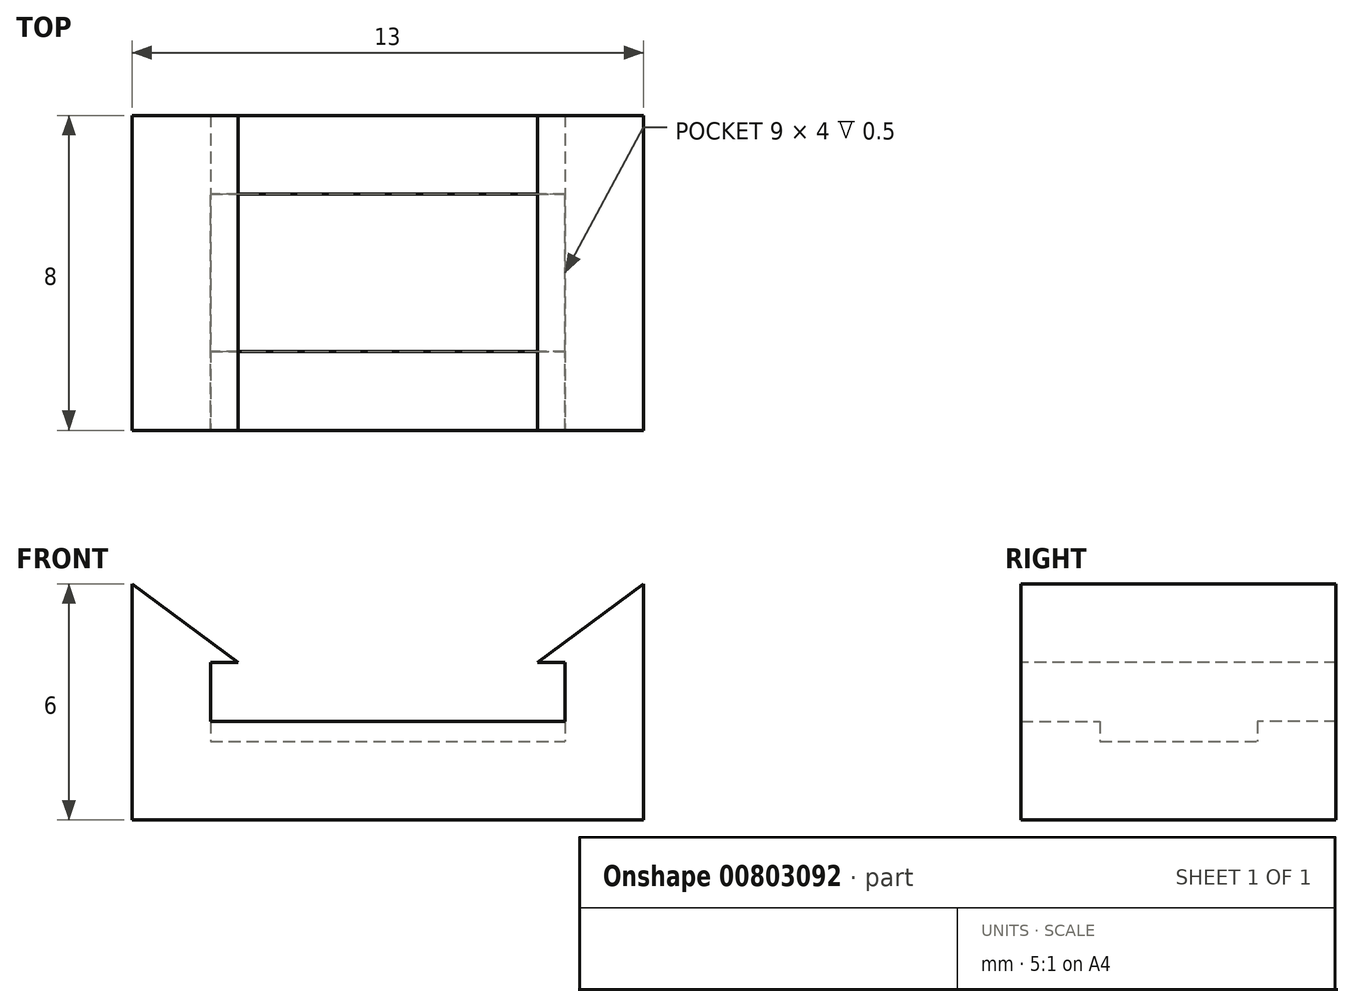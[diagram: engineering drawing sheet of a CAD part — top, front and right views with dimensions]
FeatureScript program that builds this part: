
annotation { "Feature Type Name" : "Feature", "Feature Type Description" : "" }
export const myFeature = defineFeature(function(context is Context, id is Id, definition is map)
    precondition{}
    {
        {
            var Q0;
            Q0=qCreatedBy(makeId("Top.planeOp"),FACE);
            var sketch = newSketch(context, id + "F0", { "sketchPlane" : qUnion([Q0])});
            skLineSegment(sketch, "E0.bottom", {"start": v(6.5, 4) * mm, "end": v(-6.5, 4) * mm});
            skLineSegment(sketch, "E0.top", {"start": v(6.5, -4) * mm, "end": v(-6.5, -4) * mm});
            skLineSegment(sketch, "E0.left", {"start": v(6.5, 4) * mm, "end": v(6.5, -4) * mm});
            skLineSegment(sketch, "E0.right", {"start": v(-6.5, 4) * mm, "end": v(-6.5, -4) * mm});
            skPoint(sketch, "E0.middle", {"position": v(0, 0) * mm});
            skSolve(sketch);
        }
        {
            var Q0;
            Q0=qCreatedBy(makeId("Top.planeOp"),FACE);
            var sketch = newSketch(context, id + "F1", { "sketchPlane" : qUnion([Q0])});
            skLineSegment(sketch, "E1.bottom", {"start": v(6.5, 4) * mm, "end": v(-6.5, 4) * mm});
            skLineSegment(sketch, "E1.top", {"start": v(6.5, -4) * mm, "end": v(-6.5, -4) * mm});
            skLineSegment(sketch, "E1.left", {"start": v(6.5, 4) * mm, "end": v(6.5, -4) * mm});
            skLineSegment(sketch, "E1.right", {"start": v(-6.5, 4) * mm, "end": v(-6.5, -4) * mm});
            skPoint(sketch, "E1.middle", {"position": v(0, 0) * mm});
            skLineSegment(sketch, "E2.bottom", {"start": v(4.5, 2) * mm, "end": v(-4.5, 2) * mm});
            skLineSegment(sketch, "E2.top", {"start": v(4.5, -2) * mm, "end": v(-4.5, -2) * mm});
            skLineSegment(sketch, "E2.left", {"start": v(4.5, 2) * mm, "end": v(4.5, -2) * mm});
            skLineSegment(sketch, "E2.right", {"start": v(-4.5, 2) * mm, "end": v(-4.5, -2) * mm});
            skSolve(sketch);
        }
        {
            var Q0;
            Q0=qCreatedBy(makeId("Top.planeOp"),FACE);
            var sketch = newSketch(context, id + "F2", { "sketchPlane" : qUnion([Q0])});
            skLineSegment(sketch, "E3.bottom", {"start": v(4.5, 4) * mm, "end": v(-4.5, 4) * mm});
            skLineSegment(sketch, "E3.top", {"start": v(4.5, 2) * mm, "end": v(-4.5, 2) * mm});
            skLineSegment(sketch, "E3.left", {"start": v(4.5, 4) * mm, "end": v(4.5, 2) * mm});
            skLineSegment(sketch, "E3.right", {"start": v(-4.5, 4) * mm, "end": v(-4.5, 2) * mm});
            skPoint(sketch, "E3.middle", {"position": v(0, 3) * mm});
            skPoint(sketch, "E4.MirrorP", {"position": v(0, -3) * mm});
            skLineSegment(sketch, "E5.MirrorCS", {"start": v(-4.5, -4) * mm, "end": v(-4.5, -2) * mm});
            skLineSegment(sketch, "E6.MirrorCS", {"start": v(4.5, -4) * mm, "end": v(4.5, -2) * mm});
            skLineSegment(sketch, "E7.MirrorCS", {"start": v(4.5, -2) * mm, "end": v(-4.5, -2) * mm});
            skLineSegment(sketch, "E8.MirrorCS", {"start": v(4.5, -4) * mm, "end": v(-4.5, -4) * mm});
            skSolve(sketch);
        }
        {
            var Q0;
            Q0=qSketchRegion(id+"F0",true);
            extrude(context, id + "F3", {"entities" : qUnion([Q0]), "depth" : 2 * mm, "offsetDistance" : 25 * mm});
        }
        {
            var Q0;
            Q0=qSketchRegion(id+"F1",true);
            extrude(context, id + "F4", {"entities" : qUnion([Q0]), "operationType" : NewBodyOperationType.ADD, "depth" : 4 * mm, "offsetDistance" : 25 * mm});
        }
        {
            var Q0;
            Q0=qSketchRegion(id+"F2",true);
            extrude(context, id + "F5", {"entities" : qUnion([Q0]), "operationType" : NewBodyOperationType.REMOVE, "endBound" : BoundingType.UP_TO_NEXT, "depth" : 25 * mm, "offsetDistance" : 25 * mm, "hasSecondDirection" : true, "secondDirectionOppositeDirection" : false, "secondDirectionDepth" : 2.5 * mm});
        }
        {
            var Q0;
            {var subQ0=sQuery(id+"F1.wireOp",EDGE,"E1.bottom");var subQ1=sQuery(id+"F1.wireOp",EDGE,"E1.top");var subQ2=sQuery(id+"F1.wireOp",EDGE,"E1.right");var subQ3=sQuery(id+"F1.wireOp",EDGE,"E2.right");Q0=makeQuery(id+"F5.boolean.opBoolean","SPLIT",FACE,{"disambiguationData":[TD([makeQuery(id+"F3.opExtrude","SWEPT_FACE",FACE,{"disambiguationData":[OSD([sQuery(id+"F0.wireOp",EDGE,"E0.right")])]})])],"derivedFrom":makeQuery(id+"F4.opExtrude","CAP_FACE",FACE,{"disambiguationData":[OSD([subQ0,subQ1,sQuery(id+"F1.wireOp",EDGE,"E1.left"),subQ2,sQuery(id+"F1.wireOp",EDGE,"E2.bottom"),sQuery(id+"F1.wireOp",EDGE,"E2.top"),sQuery(id+"F1.wireOp",EDGE,"E2.left"),subQ3])],"isStart":false})});}
            var sketch = newSketch(context, id + "F6", { "sketchPlane" : qUnion([Q0])});
            skLineSegment(sketch, "E9.bottom", {"start": v(-6.5, 4) * mm, "end": v(-3.8, 4) * mm});
            skLineSegment(sketch, "E9.top", {"start": v(-6.5, -4) * mm, "end": v(-3.8, -4) * mm});
            skLineSegment(sketch, "E9.left", {"start": v(-6.5, 4) * mm, "end": v(-6.5, -4) * mm});
            skLineSegment(sketch, "E9.right", {"start": v(-3.8, 4) * mm, "end": v(-3.8, -4) * mm});
            skLineSegment(sketch, "E10.MirrorCS", {"start": v(6.5, 4) * mm, "end": v(3.8, 4) * mm});
            skLineSegment(sketch, "E11.MirrorCS", {"start": v(3.8, 4) * mm, "end": v(3.8, -4) * mm});
            skLineSegment(sketch, "E12.MirrorCS", {"start": v(6.5, 4) * mm, "end": v(6.5, -4) * mm});
            skLineSegment(sketch, "E13.MirrorCS", {"start": v(6.5, -4) * mm, "end": v(3.8, -4) * mm});
            skSolve(sketch);
        }
        {
            var Q0;
            Q0=qSketchRegion(id+"F6",true);
            extrude(context, id + "F7", {"entities" : qUnion([Q0]), "operationType" : NewBodyOperationType.ADD, "depth" : 2 * mm, "offsetDistance" : 25 * mm});
        }
        {
            var Q0;
            Q0=makeQuery(id+"F7.boolean.opBoolean","MERGE",FACE,{"derivedFrom":[makeQuery(id+"F4.boolean.opBoolean","MERGE",FACE,{"derivedFrom":[makeQuery(id+"F3.opExtrude","SWEPT_FACE",FACE,{"disambiguationData":[OSD([sQuery(id+"F0.wireOp",EDGE,"E0.top")])]}),makeQuery(id+"F4.opExtrude","SWEPT_FACE",FACE,{"disambiguationData":[OSD([sQuery(id+"F1.wireOp",EDGE,"E1.top")])]})]}),makeQuery(id+"F7.opExtrude","SWEPT_FACE",FACE,{"disambiguationData":[OSD([sQuery(id+"F6.wireOp",EDGE,"E9.top")])]}),makeQuery(id+"F7.opExtrude","SWEPT_FACE",FACE,{"disambiguationData":[OSD([sQuery(id+"F6.wireOp",EDGE,"E13.MirrorCS")])]})]});
            var sketch = newSketch(context, id + "F8", { "sketchPlane" : qUnion([Q0])});
            skLineSegment(sketch, "E14", {"start": v(-6.5, 6) * mm, "end": v(-3.8, 4) * mm});
            skLineSegment(sketch, "E15", {"start": v(-3.8, 4) * mm, "end": v(-3.8, 6) * mm});
            skLineSegment(sketch, "E16", {"start": v(-3.8, 6) * mm, "end": v(-6.5, 6) * mm});
            skLineSegment(sketch, "E17.MirrorCS", {"start": v(6.5, 6) * mm, "end": v(3.8, 4) * mm});
            skLineSegment(sketch, "E18.MirrorCS", {"start": v(3.8, 4) * mm, "end": v(3.8, 6) * mm});
            skLineSegment(sketch, "E19.MirrorCS", {"start": v(3.8, 6) * mm, "end": v(6.5, 6) * mm});
            skSolve(sketch);
        }
        {
            var Q0;
            Q0=qSketchRegion(id+"F8",true);
            extrude(context, id + "F9", {"entities" : qUnion([Q0]), "operationType" : NewBodyOperationType.REMOVE, "endBound" : BoundingType.THROUGH_ALL, "oppositeDirection" : true, "depth" : 25 * mm, "offsetDistance" : 25 * mm});
        }
    });
